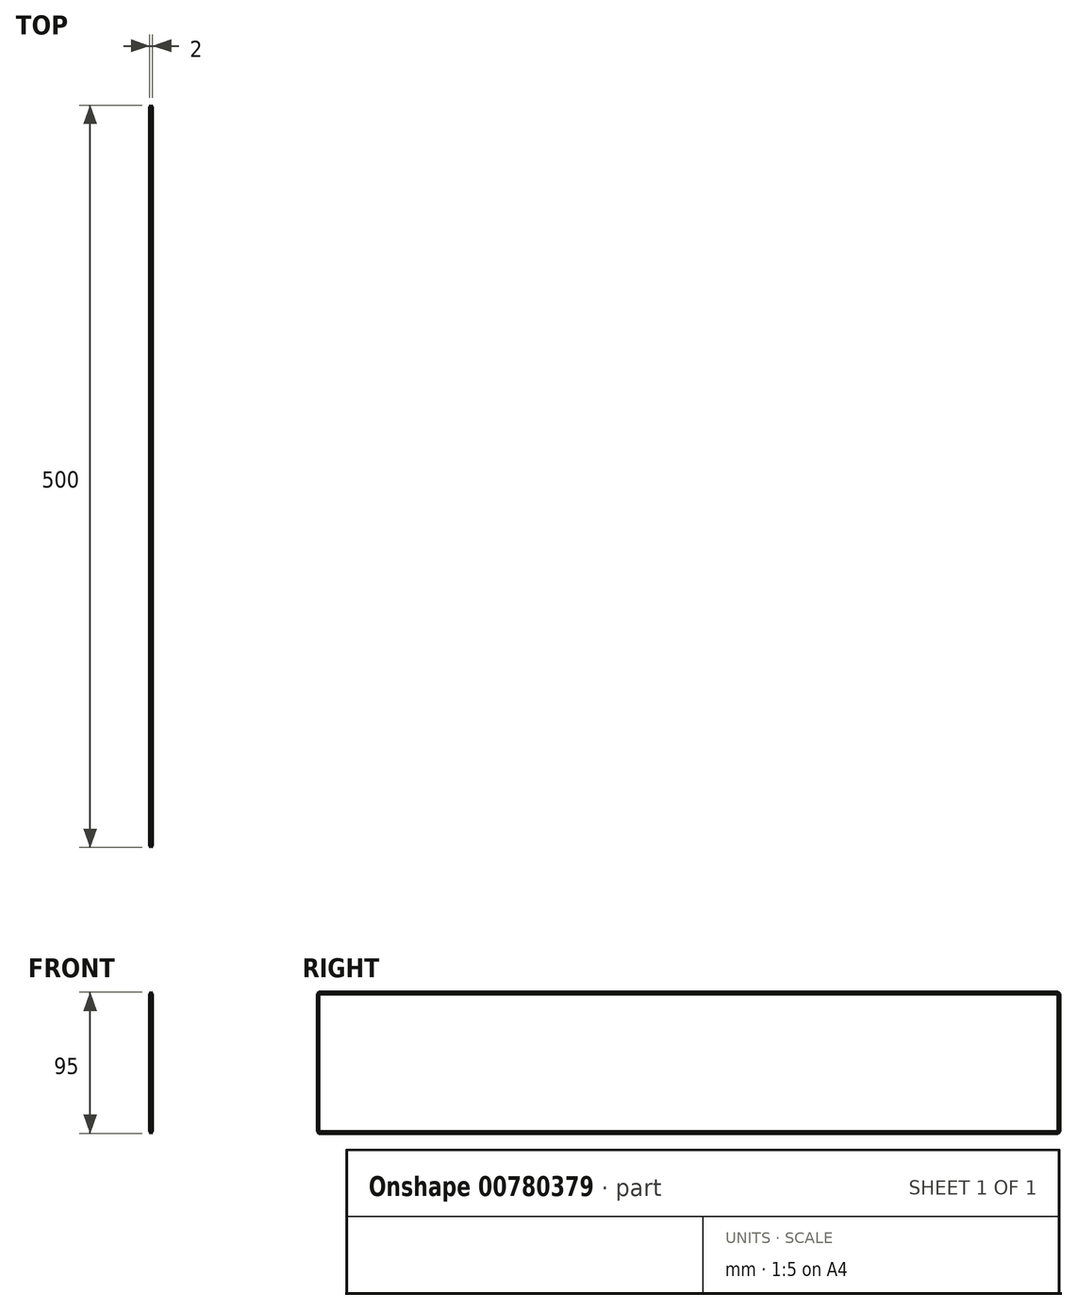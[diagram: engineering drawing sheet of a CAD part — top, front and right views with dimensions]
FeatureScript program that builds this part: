
annotation { "Feature Type Name" : "Feature", "Feature Type Description" : "" }
export const myFeature = defineFeature(function(context is Context, id is Id, definition is map)
    precondition{}
    {
        {
            var Q0;
            Q0=qCreatedBy(makeId("Right.planeOp"),FACE);
            var sketch = newSketch(context, id + "F0", { "sketchPlane" : qUnion([Q0])});
            skLineSegment(sketch, "E0.bottom", {"start": v(250, 47.5) * mm, "end": v(-250, 47.5) * mm});
            skLineSegment(sketch, "E0.top", {"start": v(250, -47.5) * mm, "end": v(-250, -47.5) * mm});
            skLineSegment(sketch, "E0.left", {"start": v(250, 47.5) * mm, "end": v(250, -47.5) * mm});
            skLineSegment(sketch, "E0.right", {"start": v(-250, 47.5) * mm, "end": v(-250, -47.5) * mm});
            skPoint(sketch, "E0.middle", {"position": v(0, 0) * mm});
            skSolve(sketch);
        }
        {
            var Q0;
            Q0=makeQuery(id+"F0.imprint","IMPRINT",FACE,{"disambiguationData":[TD([[makeQuery(id+"F0.imprint","IMPRINT",EDGE,{"derivedFrom":sQuery(id+"F0.wireOp",EDGE,"E0.bottom")}),1.0]])]});
            extrude(context, id + "F1", {"entities" : qUnion([Q0]), "depth" : 2 * mm, "offsetDistance" : 25 * mm});
        }
        {
            var Q0;
            Q0=makeQuery(id+"F1.opExtrude","CAP_EDGE",EDGE,{"disambiguationData":[OSD([sQuery(id+"F0.wireOp",EDGE,"E0.bottom")])],"isStart":false});
            var Q1;
            Q1=makeQuery(id+"F1.opExtrude","CAP_EDGE",EDGE,{"disambiguationData":[OSD([sQuery(id+"F0.wireOp",EDGE,"E0.right")])],"isStart":false});
            var Q2;
            Q2=makeQuery(id+"F1.opExtrude","CAP_EDGE",EDGE,{"disambiguationData":[OSD([sQuery(id+"F0.wireOp",EDGE,"E0.right")])],"isStart":true});
            var Q3;
            Q3=makeQuery(id+"F1.opExtrude","CAP_EDGE",EDGE,{"disambiguationData":[OSD([sQuery(id+"F0.wireOp",EDGE,"E0.bottom")])],"isStart":true});
            var Q4;
            Q4=makeQuery(id+"F1.opExtrude","CAP_EDGE",EDGE,{"disambiguationData":[OSD([sQuery(id+"F0.wireOp",EDGE,"E0.left")])],"isStart":false});
            var Q5;
            Q5=makeQuery(id+"F1.opExtrude","CAP_EDGE",EDGE,{"disambiguationData":[OSD([sQuery(id+"F0.wireOp",EDGE,"E0.top")])],"isStart":true});
            var Q6;
            Q6=makeQuery(id+"F1.opExtrude","CAP_EDGE",EDGE,{"disambiguationData":[OSD([sQuery(id+"F0.wireOp",EDGE,"E0.top")])],"isStart":false});
            var Q7;
            Q7=makeQuery(id+"F1.opExtrude","CAP_EDGE",EDGE,{"disambiguationData":[OSD([sQuery(id+"F0.wireOp",EDGE,"E0.left")])],"isStart":true});
            var Q8;
            Q8=makeQuery(id+"F1.opExtrude","SWEPT_FACE",FACE,{"disambiguationData":[OSD([sQuery(id+"F0.wireOp",EDGE,"E0.bottom")])]});
            var Q9;
            Q9=makeQuery(id+"F1.opExtrude","SWEPT_EDGE",EDGE,{"disambiguationData":[OSD([sQuery(id+"F0.wireOp",EDGE,"E0.top"),sQuery(id+"F0.wireOp",EDGE,"E0.right")])]});
            var Q10;
            Q10=makeQuery(id+"F1.opExtrude","SWEPT_EDGE",EDGE,{"disambiguationData":[OSD([sQuery(id+"F0.wireOp",EDGE,"E0.top"),sQuery(id+"F0.wireOp",EDGE,"E0.left")])]});
            chamfer(context, id + "F2", {"entities" : qUnion([Q0, Q1, Q2, Q3, Q4, Q5, Q6, Q7, Q8, Q9, Q10]), "width" : 1 * mm, "tangentPropagation" : true});
        }
    });
